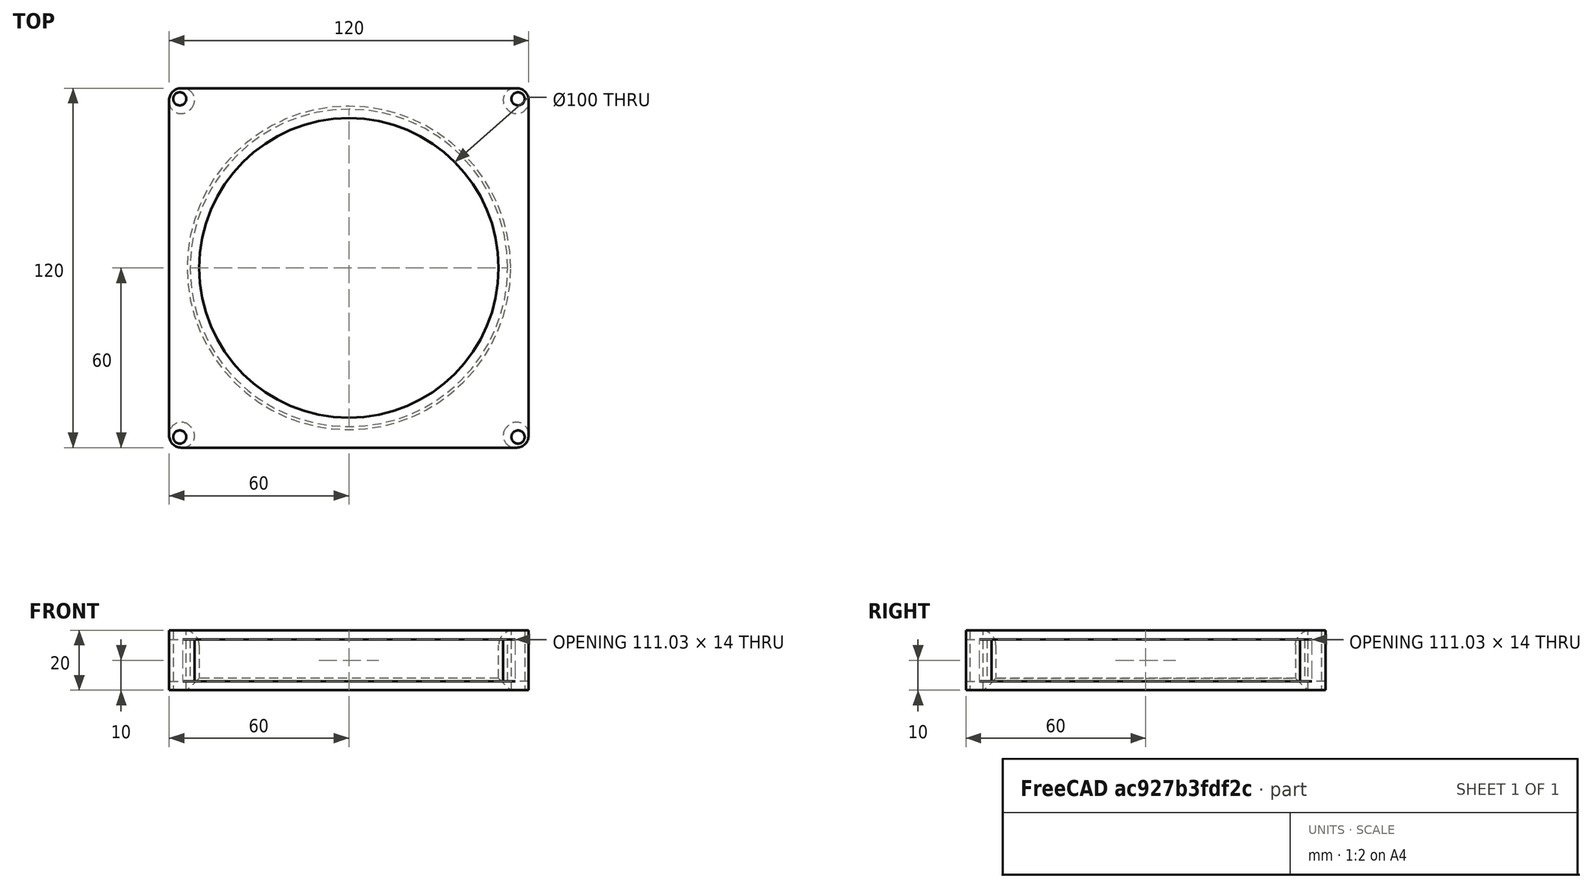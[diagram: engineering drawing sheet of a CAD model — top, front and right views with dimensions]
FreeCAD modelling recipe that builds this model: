
FCSTD DOCUMENT  (FreeCAD 0.19R23756 (Git))
Label: fan
License: All rights reserved
LicenseURL: http://en.wikipedia.org/wiki/All_rights_reserved
objects: Sketcher::SketchObject×5, PartDesign::Pocket×3, PartDesign::Fillet×3, Spreadsheet::Sheet×1, PartDesign::Pad×1, PartDesign::PolarPattern×1, PartDesign::Chamfer×1, PartDesign::Body×1, App::Part×1, Mesh::Feature×1
note: 23 computed .brp shape members not serialized (recipe doc carries the construction recipe); baked Part::Feature solids carry a one-line shape summary decoded from their .brp

FEATURE [Sketcher::SketchObject] Sketch  label="master"
  FullyConstrained = true
  MapMode = 5
  Support = -> [XY_Plane001]
  expr: Constraints[21] = <<parameters>>.inlet_radius
  expr: Constraints[22] = <<parameters>>.hole_diameter
  sketch-geometry (10):
    g0: LineSegment StartX=-60 StartY=60 StartZ=0 EndX=60 EndY=60 EndZ=0
    g1: LineSegment StartX=60 StartY=60 StartZ=0 EndX=60 EndY=-60 EndZ=0
    g2: LineSegment StartX=60 StartY=-60 StartZ=0 EndX=-60 EndY=-60 EndZ=0
    g3: LineSegment StartX=-60 StartY=-60 StartZ=0 EndX=-60 EndY=60 EndZ=0
    g4: LineSegment StartX=-56.4645 StartY=56.4645 StartZ=0 EndX=56.4645 EndY=56.4645 EndZ=0
    g5: LineSegment StartX=56.4645 StartY=56.4645 StartZ=0 EndX=56.4645 EndY=-56.4645 EndZ=0
    g6: LineSegment StartX=56.4645 StartY=-56.4645 StartZ=0 EndX=-56.4645 EndY=-56.4645 EndZ=0
    g7: LineSegment StartX=-56.4645 StartY=-56.4645 StartZ=0 EndX=-56.4645 EndY=56.4645 EndZ=0
    g8: Circle CenterX=0 CenterY=0 CenterZ=0 NormalX=0 NormalY=0 NormalZ=1 AngleXU=0 Radius=50
    g9: LineSegment StartX=-60 StartY=60 StartZ=0 EndX=-56.4645 EndY=56.4645 EndZ=0
  constraints (26):
    c: Coincident(g0,g1)
    c: Coincident(g1,g2)
    c: Coincident(g2,g3)
    c: Coincident(g3,g0)
    c: Horizontal(g0)
    c: Horizontal(g2)
    c: Vertical(g1)
    c: Vertical(g3)
    c: Equal(g0,g1)
    c: Symmetric(g2,g0,g-1)
    c: DistanceX(g0,g0) = 120  'size'
    c: Coincident(g4,g5)
    c: Coincident(g5,g6)
    c: Coincident(g6,g7)
    c: Coincident(g7,g4)
    c: Horizontal(g4)
    c: Horizontal(g6)
    c: Vertical(g5)
    c: Vertical(g7)
    c: Symmetric(g6,g4,g-1)
    c: Coincident(g8,g-1)
    c: Radius(g8) = 50
    c: Distance(g4,g0) = 5
    c: Coincident(g9,g0)
    c: Coincident(g9,g4)
    c: Angle(g4,g9) = 2.35619
FEATURE [Spreadsheet::Sheet] Spreadsheet  label="parameters"
  cells = A1=Inlet Radius; B1(inlet_radius)=50; A2=Hole Diameter; B2(hole_diameter)=5; A3=Spacer_Height; B3(height)=20; A4=Lower Flange; B4(flange_thickness_lower)=3; A5=Upper Flange; B5(flange_thickness_upper)=3; A6=Mounting Hole Radius; B6(mounting_hole_radius)=2.2; A7=Wall Thickness; B7(wall_thickness)=3
FEATURE [Sketcher::SketchObject] Sketch001
  ExternalGeometry = -> [Sketch]
  FullyConstrained = true
  MapMode = 5
  Support = -> [XY_Plane001]
  sketch-geometry (4):
    g0: LineSegment StartX=-60 StartY=60 StartZ=0 EndX=60 EndY=60 EndZ=0
    g1: LineSegment StartX=60 StartY=60 StartZ=0 EndX=60 EndY=-60 EndZ=0
    g2: LineSegment StartX=60 StartY=-60 StartZ=0 EndX=-60 EndY=-60 EndZ=0
    g3: LineSegment StartX=-60 StartY=-60 StartZ=0 EndX=-60 EndY=60 EndZ=0
  constraints (10):
    c: Coincident(g0,g1)
    c: Coincident(g1,g2)
    c: Coincident(g2,g3)
    c: Coincident(g3,g0)
    c: Horizontal(g0)
    c: Horizontal(g2)
    c: Vertical(g1)
    c: Vertical(g3)
    c: Coincident(g0,g-3)
    c: Symmetric(g0,g2,g-1)
FEATURE [PartDesign::Pad] Pad
  Direction = (1,1,1)
  Length = 20
  Length2 = 100
  Profile = -> Sketch001
  Type = 0
  expr: Length = <<parameters>>.height
FEATURE [Sketcher::SketchObject] Sketch002
  ExternalGeometry = -> [Sketch]
  FullyConstrained = true
  MapMode = 5
  Support = -> [XY_Plane001]
  sketch-geometry (1):
    g0: Circle CenterX=0 CenterY=0 CenterZ=0 NormalX=0 NormalY=0 NormalZ=1 AngleXU=0 Radius=50
  constraints (2):
    c: Coincident(g0,g-1)
    c: Equal(g0,g-3)
FEATURE [PartDesign::Pocket] Pocket
  BaseFeature = -> Pad
  Length = 5
  Length2 = 100
  Profile = -> Sketch002
  Reversed = true
  Type = 1
FEATURE [Sketcher::SketchObject] Sketch003
  ExternalGeometry = -> [Sketch]
  FullyConstrained = true
  MapMode = 5
  Support = -> [XY_Plane001]
  expr: Constraints[1] = <<parameters>>.mounting_hole_radius
  sketch-geometry (1):
    g0: Circle CenterX=-56.4645 CenterY=56.4645 CenterZ=0 NormalX=0 NormalY=0 NormalZ=1 AngleXU=0 Radius=2.2
  constraints (2):
    c: Coincident(g-4,g0)
    c: Radius(g0) = 2.2
FEATURE [PartDesign::Pocket] Pocket001
  BaseFeature = -> Pocket
  Length = 5
  Length2 = 100
  Profile = -> Sketch003
  Reversed = true
  Type = 1
FEATURE [PartDesign::PolarPattern] PolarPattern
  Angle = 360
  Axis = -> Sketch003 [N_Axis]
  BaseFeature = -> Pocket001
  Occurrences = 4
  Originals = -> [Pocket001]
FEATURE [Sketcher::SketchObject] Sketch004
  AttachmentOffset = pos=(0,0,3) rot=(0,0,1;0rad)
  ExternalGeometry = -> [Sketch]
  FullyConstrained = true
  MapMode = 5
  Placement = pos=(0,0,3) rot=(0,0,1;0rad)
  Support = -> [XY_Plane001]
  expr: .AttachmentOffset.Base.z = <<parameters>>.flange_thickness_lower
  expr: Constraints[2] = <<parameters>>.inlet_radius + <<parameters>>.wall_thickness
  sketch-geometry (3):
    g0: Circle CenterX=0 CenterY=0 CenterZ=0 NormalX=0 NormalY=0 NormalZ=1 AngleXU=0 Radius=53
    g1: Circle CenterX=0 CenterY=0 CenterZ=0 NormalX=0 NormalY=0 NormalZ=1 AngleXU=0 Radius=74.8528
    g2: Circle CenterX=-56.4645 CenterY=56.4645 CenterZ=0 NormalX=0 NormalY=0 NormalZ=1 AngleXU=0 Radius=5
  constraints (6):
    c: Coincident(g0,g-1)
    c: Coincident(g1,g0)
    c: Radius(g0) = 53
    c: Coincident(g2,g-5)
    c: PointOnObject(g-4,g2)
    c: Tangent(g1,g2)
FEATURE [PartDesign::Pocket] Pocket002
  BaseFeature = -> PolarPattern
  Length = 14
  Length2 = 100
  Profile = -> Sketch004
  Reversed = true
  Type = 0
  expr: Length = <<parameters>>.height - <<parameters>>.flange_thickness_upper - <<parameters>>.flange_thickness_lower
FEATURE [PartDesign::Fillet] Fillet
  Base = -> Pocket002 [Edge27]
  BaseFeature = -> Pocket002
  Radius = 5
  SupportTransform = false
FEATURE [PartDesign::Chamfer] Chamfer
  Angle = 45
  Base = -> Fillet [Edge45]
  BaseFeature = -> Fillet
  ChamferType = 0
  FlipDirection = false
  Size = 4
  Size2 = 1
  SupportTransform = false
FEATURE [PartDesign::Fillet] Fillet001
  Base = -> Chamfer [Edge35,Edge30,Edge24,Edge25]
  BaseFeature = -> Chamfer
  Radius = 4
  SupportTransform = false
FEATURE [PartDesign::Fillet] Fillet002
  Base = -> Fillet001 [Edge28,Edge20,Edge45,Edge34,Edge43,Edge30,Edge36,Edge18]
  BaseFeature = -> Fillet001
  Radius = 4
  SupportTransform = false
FEATURE [PartDesign::Body] Body
  Group = -> [Sketch,Sketch001,Pad,Sketch002,Pocket,Sketch003,Pocket001,PolarPattern,Sketch004,Pocket002,Fillet,Chamfer,Fillet001,Fillet002]
  Origin = -> Origin001
  Tip = -> Fillet002
FEATURE [App::Part] Part
  Group = -> [Body]
  Origin = -> Origin
FEATURE [Mesh::Feature] Mesh  label="Fillet002 (Meshed)"
